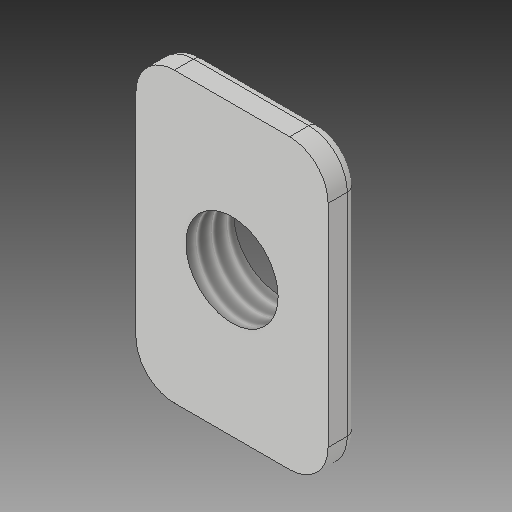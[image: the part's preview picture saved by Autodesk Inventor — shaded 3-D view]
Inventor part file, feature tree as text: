
AUTODESK INVENTOR PART (.ipt)
format: ipt  version: 2017 (Build 210142000, 142)  size: 158,720 bytes
history: native  units: mm
features: other x3, sketch x2
ambient origin geometry x8: Origin, YZ Plane, XZ Plane, XY Plane, X Axis, Y Axis, Z Axis, Center Point
bodies: Solid1 (feature_tree)
feature tree (5):
  other  "M5 Tee Nut-Generic_MIR_MIR.ipt"
  other  "Solid1::M5 Tee Nut-Generic_MIR_MIR.ipt"
  other  "TaggingFeature1"
  sketch  "Sketch1"  dims[d0=10.0mm]
  sketch  "Sketch2"
